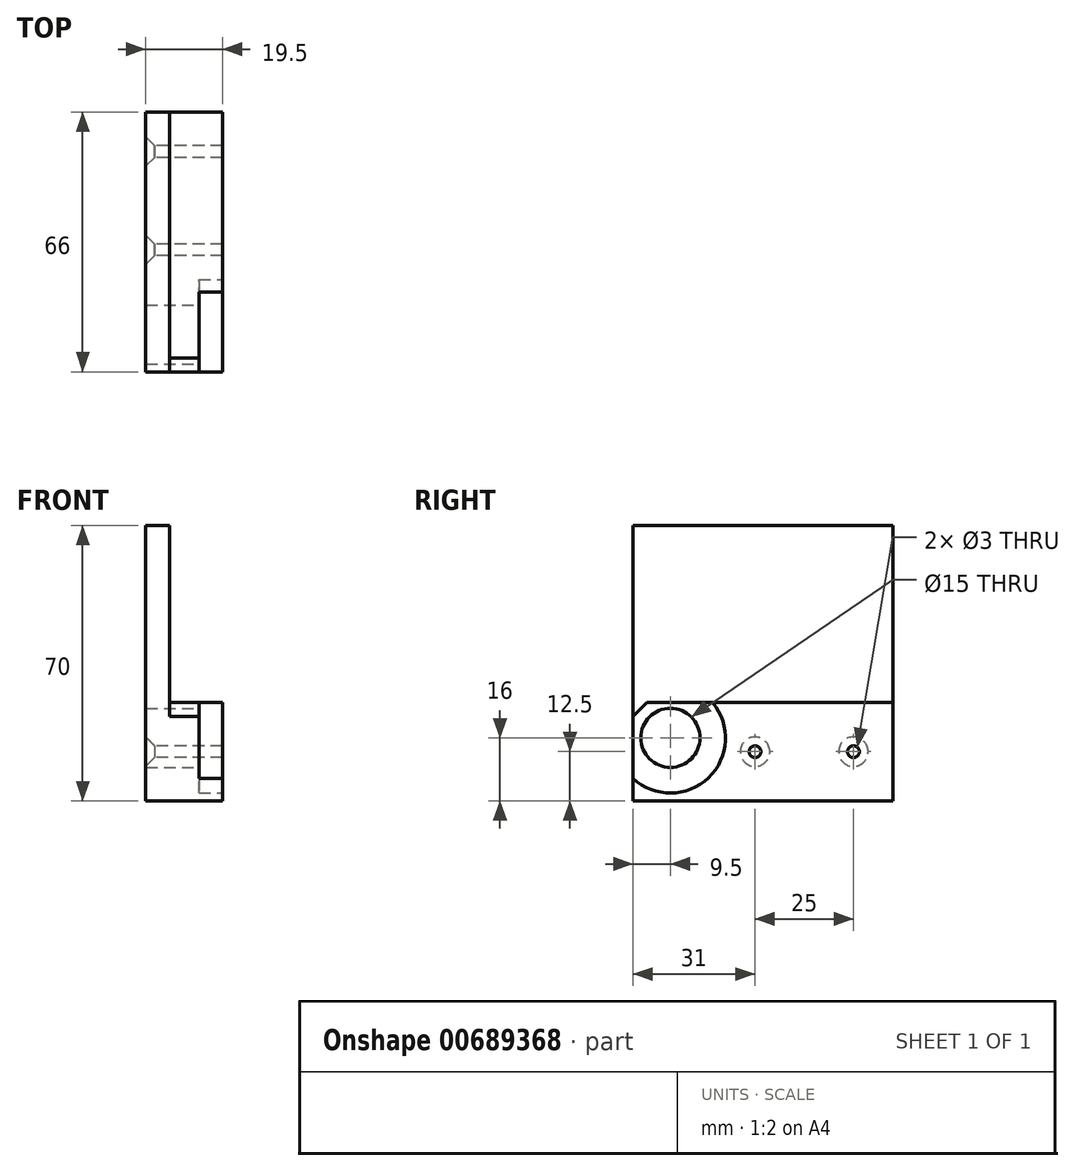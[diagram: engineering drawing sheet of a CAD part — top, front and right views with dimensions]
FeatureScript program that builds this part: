
annotation { "Feature Type Name" : "Feature", "Feature Type Description" : "" }
export const myFeature = defineFeature(function(context is Context, id is Id, definition is map)
    precondition{}
    {
        {
            var Q0;
            Q0=qCreatedBy(makeId("Front.planeOp"),FACE);
            var sketch = newSketch(context, id + "F0", { "sketchPlane" : qUnion([Q0])});
            skLineSegment(sketch, "E0", {"start": v(0, 0) * mm, "end": v(0, 70) * mm});
            skLineSegment(sketch, "E1", {"start": v(0, 0) * mm, "end": v(19.5, 0) * mm});
            skLineSegment(sketch, "E2", {"start": v(19.5, 25) * mm, "end": v(6, 25) * mm});
            skLineSegment(sketch, "E3", {"start": v(6, 70) * mm, "end": v(6, 25) * mm});
            skLineSegment(sketch, "E4", {"start": v(0, 70) * mm, "end": v(6, 70) * mm});
            skLineSegment(sketch, "E5", {"start": v(19.5, 0) * mm, "end": v(19.5, 25) * mm});
            skSolve(sketch);
        }
        {
            var Q0;
            Q0=qSketchRegion(id+"F0",true);
            extrude(context, id + "F1", {"entities" : qUnion([Q0]), "depth" : 66 * mm});
        }
        {
            var Q0;
            Q0=makeQuery(id+"F1.opExtrude","SWEPT_FACE",FACE,{"disambiguationData":[OSD([sQuery(id+"F0.wireOp",EDGE,"E5")])]});
            var sketch = newSketch(context, id + "F2", { "sketchPlane" : qUnion([Q0])});
            skLineSegment(sketch, "E6", {"start": v(-33, 36.84) * mm, "end": v(-33, -7.5) * mm, "construction": true});
            skLineSegment(sketch, "E7", {"start": v(9.43, 28) * mm, "end": v(-80.2, 28) * mm, "construction": true});
            skLineSegment(sketch, "E8", {"start": v(9.43, 16) * mm, "end": v(-79.93, 16) * mm, "construction": true});
            skLineSegment(sketch, "E9", {"start": v(-71, 47.6) * mm, "end": v(-71, -9.4) * mm, "construction": true});
            skLineSegment(sketch, "E10", {"start": v(-56.5, 16.24) * mm, "end": v(-56.5, 4.24) * mm, "construction": true});
            skCircle(sketch, "E11", {"center": v(-56.5, 16) * mm, "radius": 7.5 * mm});
            skLineSegment(sketch, "E12", {"start": v(5, 48.77) * mm, "end": v(5, -8.97) * mm, "construction": true});
            skLineSegment(sketch, "E13", {"start": v(-9.5, 16.43) * mm, "end": v(-9.5, 4.8) * mm, "construction": true});
            skSolve(sketch);
        }
        {
            var Q0;
            Q0=qSketchRegion(id+"F2",true);
            extrude(context, id + "F3", {"entities" : qUnion([Q0]), "operationType" : NewBodyOperationType.REMOVE, "endBound" : BoundingType.THROUGH_ALL, "oppositeDirection" : true, "depth" : 25 * mm});
        }
        {
            var Q0;
            Q0=makeQuery(id+"F1.opExtrude","SWEPT_FACE",FACE,{"disambiguationData":[OSD([sQuery(id+"F0.wireOp",EDGE,"E5")])]});
            var sketch = newSketch(context, id + "F4", { "sketchPlane" : qUnion([Q0])});
            skPoint(sketch, "E14.start.orphan", {"position": v(-56.5, 16) * mm});
            skPoint(sketch, "E15.orphan", {"position": v(-44.75, 0) * mm});
            skPoint(sketch, "E16.orphan", {"position": v(-43.5, 0) * mm});
            skLineSegment(sketch, "E17", {"start": v(-66, 25) * mm, "end": v(-45.78, 25) * mm});
            skLineSegment(sketch, "E18", {"start": v(-66, 25) * mm, "end": v(-66, 0) * mm});
            skArc(sketch, "E19.converted", {"start": v(-66, 5.72) * mm, "mid": v(-46.84, 5.87) * mm, "end": v(-45.78, 25) * mm});
            skSolve(sketch);
        }
        {
            var Q0;
            Q0=qSketchRegion(id+"F4",true);
            extrude(context, id + "F5", {"entities" : qUnion([Q0]), "operationType" : NewBodyOperationType.REMOVE, "oppositeDirection" : true, "depth" : 6 * mm});
        }
        {
            var Q0;
            Q0=makeQuery(id+"F5.boolean.opBoolean","COPY",FACE,{"derivedFrom":makeQuery(id+"F5.opExtrude","CAP_FACE",FACE,{"disambiguationData":[OSD([sQuery(id+"F4.wireOp",EDGE,"E17"),sQuery(id+"F4.wireOp",EDGE,"E18"),sQuery(id+"F4.wireOp",EDGE,"E19.converted")])],"isStart":false})});
            var sketch = newSketch(context, id + "F6", { "sketchPlane" : qUnion([Q0])});
            skLineSegment(sketch, "E20", {"start": v(-66, 25) * mm, "end": v(-62.5, 25) * mm});
            skLineSegment(sketch, "E21", {"start": v(-62.5, 25) * mm, "end": v(-66, 21.5) * mm});
            skLineSegment(sketch, "E22", {"start": v(-66, 25) * mm, "end": v(-66, 21.5) * mm});
            skSolve(sketch);
        }
        {
            var Q0;
            Q0=qSketchRegion(id+"F6",true);
            extrude(context, id + "F7", {"entities" : qUnion([Q0]), "operationType" : NewBodyOperationType.REMOVE, "oppositeDirection" : true, "depth" : 7.5 * mm});
        }
        {
            var Q0;
            Q0=makeQuery(id+"F1.opExtrude","SWEPT_FACE",FACE,{"disambiguationData":[OSD([sQuery(id+"F0.wireOp",EDGE,"E0")])]});
            var sketch = newSketch(context, id + "F8", { "sketchPlane" : qUnion([Q0])});
            skPoint(sketch, "E23", {"position": v(10, 12.5) * mm});
            skPoint(sketch, "E24", {"position": v(35, 12.5) * mm});
            skSolve(sketch);
        }
        {
            var Q0;
            Q0=sQuery(id+"F8.wireOp",VERTEX,"E23");
            var Q1;
            Q1=sQuery(id+"F8.wireOp",VERTEX,"E24");
            var Q2;
            Q2=makeQuery(id+"F1.opExtrude","SWEPT_BODY",BODY,{"disambiguationData":[OSD([sQuery(id+"F0.wireOp",EDGE,"E0"),sQuery(id+"F0.wireOp",EDGE,"E1"),sQuery(id+"F0.wireOp",EDGE,"E2"),sQuery(id+"F0.wireOp",EDGE,"E3"),sQuery(id+"F0.wireOp",EDGE,"E4"),sQuery(id+"F0.wireOp",EDGE,"E5")])]});
            hole(context, id + "F9", {"style" : HoleStyle.C_SINK, "endStyle" : HoleEndStyle.THROUGH, "holeDiameter" : 3 * mm, "cSinkDiameter" : 7.5 * mm, "cSinkAngle" : 90 * degree, "majorDiameter" : 5 * mm, "isTappedThrough" : true, "tappedDepth" : 12 * mm, "tapClearance" : 3, "startFromSketch" : true, "locations" : qUnion([Q0, Q1]), "scope" : qUnion([Q2])});
        }
    });
